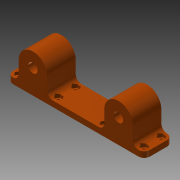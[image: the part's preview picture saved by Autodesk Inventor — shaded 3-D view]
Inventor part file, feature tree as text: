
AUTODESK INVENTOR PART (.ipt)
format: ipt  version: 2013 (Build 170138000, 138)  size: 239,104 bytes
history: native  units: mm
features: extrude x3, sketch x3, projected_geometry x3, fillet x2
ambient origin geometry x8: Origin, YZ Plane, XZ Plane, XY Plane, X Axis, Y Axis, Z Axis, Center Point
bodies: Solid1 (feature_tree)
feature tree (11):
  extrude  "Extrusion1"  Depth=21.0mm
  extrude  "Extrusion2"  Depth=8.1mm
  extrude  "Extrusion3"  Depth=25.0mm TaperAngle=0.0deg
  fillet  "Fillet1"  Radius=10.0mm
  fillet  "Fillet2"  Radius=5.0mm
  sketch  "Sketch1"  dims[d0=5.0mm d2=21.0mm]
  sketch  "Sketch2"  dims[d3=12.5mm d4=8.1mm]
  projected_geometry  "Projected Loop1"
  projected_geometry  "Projected Loop2"
  sketch  "Sketch3"  dims[d5=75.0mm d6=25.0mm d7=0.0mm d8=10.0mm d9=5.0mm d10=5.0mm d11=3.1mm d12=2.5mm d13=0.0mm d14=5.6mm d15=2.5mm d16=0.0mm d17=5.0mm d18=5.0mm]
  projected_geometry  "Project Cut Edges1"
